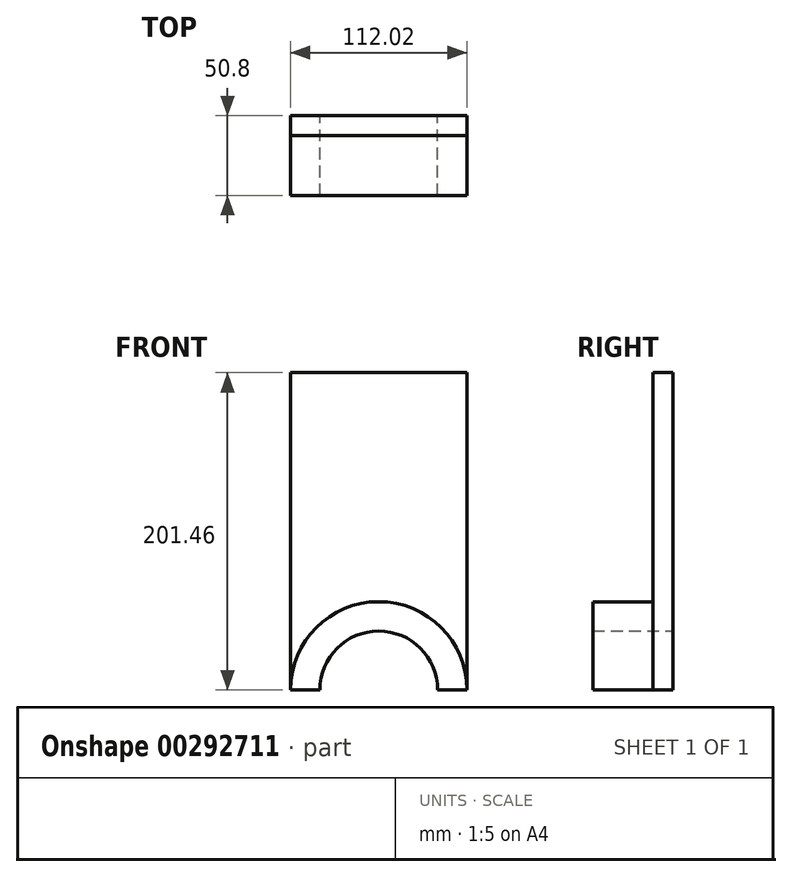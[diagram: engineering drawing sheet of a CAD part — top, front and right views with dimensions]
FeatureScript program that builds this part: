
annotation { "Feature Type Name" : "Feature", "Feature Type Description" : "" }
export const myFeature = defineFeature(function(context is Context, id is Id, definition is map)
    precondition{}
    {
        {
            var Q0;
            Q0=qCreatedBy(makeId("Front.planeOp"),FACE);
            var sketch = newSketch(context, id + "F0", { "sketchPlane" : qUnion([Q0])});
            skCircle(sketch, "E0", {"center": v(0, 0) * mm, "radius": 37.37 * mm});
            skCircle(sketch, "E1", {"center": v(0, 0) * mm, "radius": 56.01 * mm});
            skLineSegment(sketch, "E2", {"start": v(-37.37, 0) * mm, "end": v(-56.01, 0) * mm});
            skLineSegment(sketch, "E3", {"start": v(37.37, 0) * mm, "end": v(56.01, 0) * mm});
            skSolve(sketch);
        }
        {
            var Q0;
            Q0=qCreatedBy(makeId("Front.planeOp"),FACE);
            var sketch = newSketch(context, id + "F1", { "sketchPlane" : qUnion([Q0])});
            skLineSegment(sketch, "E4.bottom", {"start": v(56.01, 0) * mm, "end": v(-56.01, 0) * mm});
            skLineSegment(sketch, "E4.top", {"start": v(56.01, 201.46) * mm, "end": v(-56.01, 201.46) * mm});
            skLineSegment(sketch, "E4.left", {"start": v(56.01, 0) * mm, "end": v(56.01, 201.46) * mm});
            skLineSegment(sketch, "E4.right", {"start": v(-56.01, 0) * mm, "end": v(-56.01, 201.46) * mm});
            skSolve(sketch);
        }
        {
            var Q0;
            Q0 = qSketchRegion(id + "F1", true);
            extrude(context, id + "F2", {"entities" : qUnion([Q0]), "depth" : 12.7 * mm});
        }
        {
            var Q0;
            {var subQ0=sQuery(id+"F0.wireOp",EDGE,"E2");Q0=makeQuery(id+"F0.imprint","IMPRINT",FACE,{"disambiguationData":[TD([[makeQuery(id+"F0.imprint","IMPRINT",EDGE,{"derivedFrom":subQ0}),-1.0]])]});}
            extrude(context, id + "F3", {"entities" : qUnion([Q0]), "operationType" : NewBodyOperationType.ADD, "depth" : 50.8 * mm});
        }
        {
            var Q0;
            {var subQ0=sQuery(id+"F1.wireOp",EDGE,"E4.bottom");Q0=makeQuery(id+"F3.boolean.opBoolean","SPLIT",FACE,{"disambiguationData":[TD([makeQuery(id+"F3.opExtrude","SWEPT_FACE",FACE,{"disambiguationData":[OSD([sQuery(id+"F0.wireOp",EDGE,"E0")])]})])],"derivedFrom":makeQuery(id+"F2.opExtrude","CAP_FACE",FACE,{"disambiguationData":[OSD([subQ0,sQuery(id+"F1.wireOp",EDGE,"E4.top"),sQuery(id+"F1.wireOp",EDGE,"E4.left"),sQuery(id+"F1.wireOp",EDGE,"E4.right")])],"isStart":false})});}
            extrude(context, id + "F4", {"entities" : qUnion([Q0]), "operationType" : NewBodyOperationType.REMOVE, "oppositeDirection" : true, "depth" : 25.4 * mm});
        }
    });
